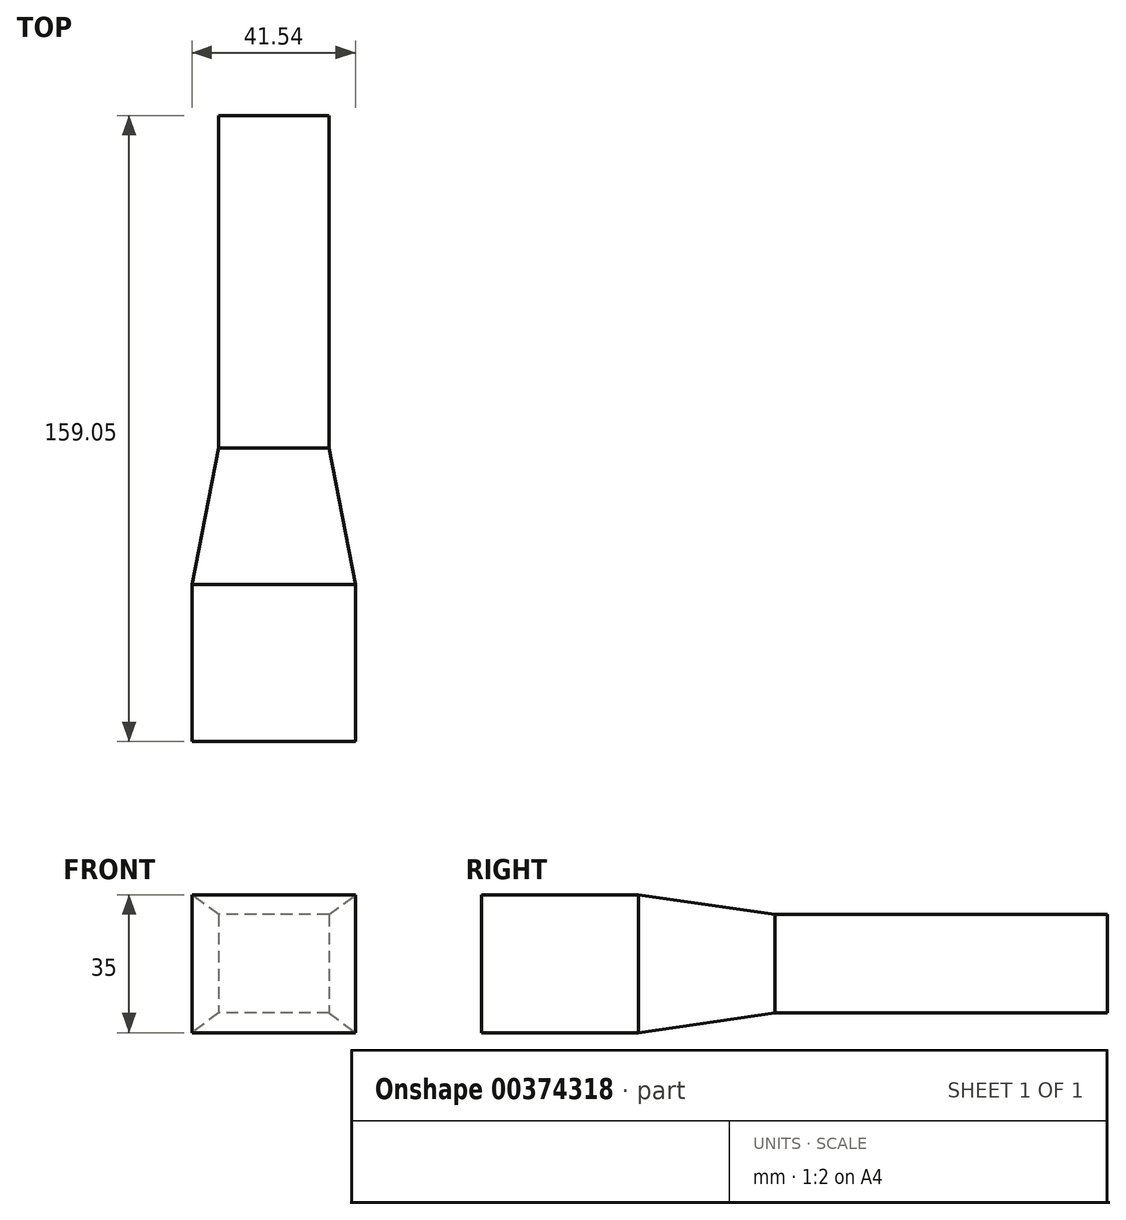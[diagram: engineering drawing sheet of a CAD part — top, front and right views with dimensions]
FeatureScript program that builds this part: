
annotation { "Feature Type Name" : "Feature", "Feature Type Description" : "" }
export const myFeature = defineFeature(function(context is Context, id is Id, definition is map)
    precondition{}
    {
        {
            var Q0;
            Q0=qCreatedBy(makeId("Top.planeOp"),FACE);
            var sketch = newSketch(context, id + "F0", { "sketchPlane" : qUnion([Q0])});
            skLineSegment(sketch, "E0.bottom", {"start": v(-27.16, 84.47) * mm, "end": v(-55.16, 84.47) * mm});
            skLineSegment(sketch, "E0.top", {"start": v(-27.16, 0) * mm, "end": v(-55.16, 0) * mm});
            skLineSegment(sketch, "E0.left", {"start": v(-27.16, 84.47) * mm, "end": v(-27.16, 0) * mm});
            skLineSegment(sketch, "E0.right", {"start": v(-55.16, 84.47) * mm, "end": v(-55.16, 0) * mm});
            skLineSegment(sketch, "E1", {"start": v(-55.16, 0) * mm, "end": v(-41.16, 0) * mm});
            skLineSegment(sketch, "E2.bottom", {"start": v(-20.39, -74.58) * mm, "end": v(-61.93, -74.58) * mm});
            skLineSegment(sketch, "E2.top", {"start": v(-20.39, -34.67) * mm, "end": v(-61.93, -34.67) * mm});
            skLineSegment(sketch, "E2.left", {"start": v(-20.39, -74.58) * mm, "end": v(-20.39, -34.67) * mm});
            skLineSegment(sketch, "E2.right", {"start": v(-61.93, -74.58) * mm, "end": v(-61.93, -34.67) * mm});
            skPoint(sketch, "E2.middle", {"position": v(-41.16, -54.62) * mm});
            skSolve(sketch);
        }
        {
            var Q0;
            Q0=makeQuery(id+"F0.imprint","IMPRINT",FACE,{"disambiguationData":[TD([[makeQuery(id+"F0.imprint","IMPRINT",EDGE,{"derivedFrom":sQuery(id+"F0.wireOp",EDGE,"E0.bottom")}),1.0]])]});
            extrude(context, id + "F1", {"entities" : qUnion([Q0]), "endBound" : BoundingType.SYMMETRIC, "depth" : 25 * mm});
        }
        {
            var Q0;
            Q0=makeQuery(id+"F0.imprint","IMPRINT",FACE,{"disambiguationData":[TD([[makeQuery(id+"F0.imprint","IMPRINT",EDGE,{"derivedFrom":sQuery(id+"F0.wireOp",EDGE,"E2.bottom")}),-1.0]])]});
            extrude(context, id + "F2", {"entities" : qUnion([Q0]), "endBound" : BoundingType.SYMMETRIC, "depth" : 35 * mm});
        }
        {
            var Q0;
            Q0=makeQuery(id+"F0.imprint","IMPRINT",FACE,{"disambiguationData":[TD([[makeQuery(id+"F0.imprint","IMPRINT",EDGE,{"derivedFrom":sQuery(id+"F0.wireOp",EDGE,"E2.bottom")}),-1.0]])]});
            extrude(context, id + "F3", {"entities" : qUnion([Q0]), "endBound" : BoundingType.SYMMETRIC, "depth" : 35 * mm});
        }
        {
            var Q0;
            Q0=makeQuery(id+"F1.opExtrude","SWEPT_FACE",FACE,{"disambiguationData":[OSD([sQuery(id+"F0.wireOp",EDGE,"E0.top"),sQuery(id+"F0.wireOp",EDGE,"E1")])]});
            var Q1;
            Q1=makeQuery(id+"F3.opExtrude","SWEPT_FACE",FACE,{"disambiguationData":[OSD([sQuery(id+"F0.wireOp",EDGE,"E2.top")])]});
            loft(context, id + "F4", {"sheetProfilesArray" : [{ "sheetProfileEntities" : qUnion([Q0]) }, { "sheetProfileEntities" : qUnion([Q1]) }]});
        }
    });
